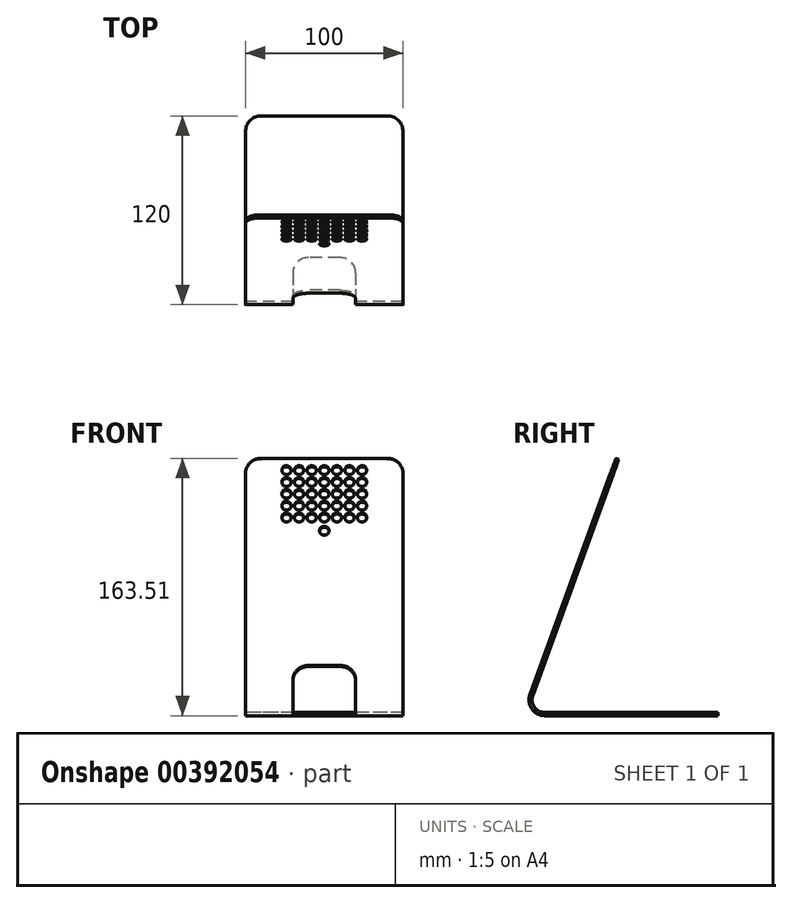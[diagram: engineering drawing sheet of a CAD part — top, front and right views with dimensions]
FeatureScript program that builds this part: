
annotation { "Feature Type Name" : "Feature", "Feature Type Description" : "" }
export const myFeature = defineFeature(function(context is Context, id is Id, definition is map)
    precondition{}
    {
        {
            var Q0;
            Q0=qCreatedBy(makeId("Right.planeOp"),FACE);
            var sketch = newSketch(context, id + "F0", { "sketchPlane" : qUnion([Q0])});
            skLineSegment(sketch, "E0", {"start": v(59.51, 163.5) * mm, "end": v(4.88, 13.42) * mm});
            skLineSegment(sketch, "E1", {"start": v(14.28, 0) * mm, "end": v(124.28, 0) * mm});
            skPoint(sketch, "E2.visualSharp", {"position": v(0, 0) * mm});
            skArc(sketch, "E2.filletArc", {"start": v(4.88, 13.42) * mm, "mid": v(6.09, 4.26) * mm, "end": v(14.28, 0) * mm});
            skLineSegment(sketch, "E3", {"start": v(4.28, 163.5) * mm, "end": v(4.28, 0) * mm, "construction": true});
            skLineSegment(sketch, "E4.0", {"start": v(14.28, 2) * mm, "end": v(124.28, 2) * mm});
            skArc(sketch, "E4.1", {"start": v(6.76, 12.74) * mm, "mid": v(7.73, 5.41) * mm, "end": v(14.28, 2) * mm});
            skLineSegment(sketch, "E4.2", {"start": v(61.4, 162.82) * mm, "end": v(6.76, 12.74) * mm});
            skLineSegment(sketch, "E5", {"start": v(59.51, 163.5) * mm, "end": v(61.4, 162.82) * mm});
            skLineSegment(sketch, "E6", {"start": v(124.28, 2) * mm, "end": v(124.28, 0) * mm});
            skSolve(sketch);
        }
        {
            var Q0;
            Q0 = qSketchRegion(id + "F0", true);
            extrude(context, id + "F1", {"entities" : qUnion([Q0]), "endBound" : BoundingType.SYMMETRIC, "depth" : 100 * mm});
        }
        {
            var Q0;
            Q0=makeQuery(id+"F1.opExtrude","CAP_EDGE",EDGE,{"disambiguationData":[OSD([sQuery(id+"F0.wireOp",EDGE,"E5")])],"isStart":true});
            var Q1;
            Q1=makeQuery(id+"F1.opExtrude","CAP_EDGE",EDGE,{"disambiguationData":[OSD([sQuery(id+"F0.wireOp",EDGE,"E5")])],"isStart":false});
            var Q2;
            Q2=makeQuery(id+"F1.opExtrude","CAP_EDGE",EDGE,{"disambiguationData":[OSD([sQuery(id+"F0.wireOp",EDGE,"E6")])],"isStart":false});
            var Q3;
            Q3=makeQuery(id+"F1.opExtrude","CAP_EDGE",EDGE,{"disambiguationData":[OSD([sQuery(id+"F0.wireOp",EDGE,"E6")])],"isStart":true});
            fillet(context, id + "F2", {"entities" : qUnion([Q0, Q1, Q2, Q3]), "radius" : 10 * mm, "tangentPropagation" : true, "allowEdgeOverflow" : false});
        }
        {
            var Q0;
            Q0=makeQuery(id+"F1.opExtrude","SWEPT_FACE",FACE,{"disambiguationData":[OSD([sQuery(id+"F0.wireOp",EDGE,"E0")])]});
            var sketch = newSketch(context, id + "F3", { "sketchPlane" : qUnion([Q0])});
            skPoint(sketch, "E7", {"position": v(0, 125) * mm});
            skSolve(sketch);
        }
        {
            var Q0;
            Q0=sQuery(id+"F3.wireOp",VERTEX,"E7");
            var Q1;
            Q1=makeQuery(id+"F1.opExtrude","SWEPT_BODY",BODY,{"disambiguationData":[OSD([sQuery(id+"F0.wireOp",EDGE,"E0"),sQuery(id+"F0.wireOp",EDGE,"E1"),sQuery(id+"F0.wireOp",EDGE,"E2.filletArc"),sQuery(id+"F0.wireOp",EDGE,"E4.0"),sQuery(id+"F0.wireOp",EDGE,"E4.1"),sQuery(id+"F0.wireOp",EDGE,"E4.2"),sQuery(id+"F0.wireOp",EDGE,"E5"),sQuery(id+"F0.wireOp",EDGE,"E6")])]});
            hole(context, id + "F4", {"style" : HoleStyle.SIMPLE, "endStyle" : HoleEndStyle.THROUGH, "holeDiameter" : 6 * mm, "isTappedThrough" : true, "tappedDepth" : 12 * mm, "tapClearance" : 3, "locations" : qUnion([Q0]), "scope" : qUnion([Q1])});
        }
        {
            var Q0;
            {var subQ0=sQuery(id+"F0.wireOp",EDGE,"E0");Q0=makeQuery(id+"F3.imprint","IMPRINT",FACE,{"disambiguationData":[TD([[makeQuery(id+"F3.imprint","IMPRINT",EDGE,{"derivedFrom":makeQuery(id+"F1.opExtrude","CAP_EDGE",EDGE,{"disambiguationData":[OSD([subQ0])],"isStart":true})}),1.0]])]});}
            var sketch = newSketch(context, id + "F5", { "sketchPlane" : qUnion([Q0])});
            skLineSegment(sketch, "E8.bottom", {"start": v(-28, 169) * mm, "end": v(28, 169) * mm, "construction": true});
            skLineSegment(sketch, "E8.top", {"start": v(-28, 131) * mm, "end": v(28, 131) * mm, "construction": true});
            skLineSegment(sketch, "E8.left", {"start": v(-28, 169) * mm, "end": v(-28, 131) * mm, "construction": true});
            skLineSegment(sketch, "E8.right", {"start": v(28, 169) * mm, "end": v(28, 131) * mm, "construction": true});
            skLineSegment(sketch, "E9", {"start": v(0, 169) * mm, "end": v(0, 131) * mm, "construction": true});
            skPoint(sketch, "E9.endSnap0", {"position": v(0, 131) * mm});
            skCircle(sketch, "E10", {"center": v(-24, 134) * mm, "radius": 3 * mm});
            skCircle(sketch, "E11.0.1.0", {"center": v(-24, 142) * mm, "radius": 3 * mm});
            skCircle(sketch, "E11.0.2.0", {"center": v(-24, 150) * mm, "radius": 3 * mm});
            skCircle(sketch, "E11.0.3.0", {"center": v(-24, 158) * mm, "radius": 3 * mm});
            skCircle(sketch, "E11.0.4.0", {"center": v(-24, 166) * mm, "radius": 3 * mm});
            skCircle(sketch, "E11.1.0.0", {"center": v(-16, 134) * mm, "radius": 3 * mm});
            skCircle(sketch, "E11.1.1.0", {"center": v(-16, 142) * mm, "radius": 3 * mm});
            skCircle(sketch, "E11.1.2.0", {"center": v(-16, 150) * mm, "radius": 3 * mm});
            skCircle(sketch, "E11.1.3.0", {"center": v(-16, 158) * mm, "radius": 3 * mm});
            skCircle(sketch, "E11.1.4.0", {"center": v(-16, 166) * mm, "radius": 3 * mm});
            skCircle(sketch, "E11.2.0.0", {"center": v(-8, 134) * mm, "radius": 3 * mm});
            skCircle(sketch, "E11.2.1.0", {"center": v(-8, 142) * mm, "radius": 3 * mm});
            skCircle(sketch, "E11.2.2.0", {"center": v(-8, 150) * mm, "radius": 3 * mm});
            skCircle(sketch, "E11.2.3.0", {"center": v(-8, 158) * mm, "radius": 3 * mm});
            skCircle(sketch, "E11.2.4.0", {"center": v(-8, 166) * mm, "radius": 3 * mm});
            skCircle(sketch, "E11.3.0.0", {"center": v(0, 134) * mm, "radius": 3 * mm});
            skCircle(sketch, "E11.3.1.0", {"center": v(0, 142) * mm, "radius": 3 * mm});
            skCircle(sketch, "E11.3.2.0", {"center": v(0, 150) * mm, "radius": 3 * mm});
            skCircle(sketch, "E11.3.3.0", {"center": v(0, 158) * mm, "radius": 3 * mm});
            skCircle(sketch, "E11.3.4.0", {"center": v(0, 166) * mm, "radius": 3 * mm});
            skCircle(sketch, "E11.4.0.0", {"center": v(8, 134) * mm, "radius": 3 * mm});
            skCircle(sketch, "E11.4.1.0", {"center": v(8, 142) * mm, "radius": 3 * mm});
            skCircle(sketch, "E11.4.2.0", {"center": v(8, 150) * mm, "radius": 3 * mm});
            skCircle(sketch, "E11.4.3.0", {"center": v(8, 158) * mm, "radius": 3 * mm});
            skCircle(sketch, "E11.4.4.0", {"center": v(8, 166) * mm, "radius": 3 * mm});
            skCircle(sketch, "E11.5.0.0", {"center": v(16, 134) * mm, "radius": 3 * mm});
            skCircle(sketch, "E11.5.1.0", {"center": v(16, 142) * mm, "radius": 3 * mm});
            skCircle(sketch, "E11.5.2.0", {"center": v(16, 150) * mm, "radius": 3 * mm});
            skCircle(sketch, "E11.5.3.0", {"center": v(16, 158) * mm, "radius": 3 * mm});
            skCircle(sketch, "E11.5.4.0", {"center": v(16, 166) * mm, "radius": 3 * mm});
            skCircle(sketch, "E11.6.0.0", {"center": v(24, 134) * mm, "radius": 3 * mm});
            skCircle(sketch, "E11.6.1.0", {"center": v(24, 142) * mm, "radius": 3 * mm});
            skCircle(sketch, "E11.6.2.0", {"center": v(24, 150) * mm, "radius": 3 * mm});
            skCircle(sketch, "E11.6.3.0", {"center": v(24, 158) * mm, "radius": 3 * mm});
            skCircle(sketch, "E11.6.4.0", {"center": v(24, 166) * mm, "radius": 3 * mm});
            skLineSegment(sketch, "E11.direction1", {"start": v(-24, 134) * mm, "end": v(-16, 134) * mm, "construction": true});
            skLineSegment(sketch, "E11.direction2", {"start": v(-24, 134) * mm, "end": v(-24, 142) * mm, "construction": true});
            skSolve(sketch);
        }
        {
            var Q0;
            Q0 = qSketchRegion(id + "F5", true);
            extrude(context, id + "F6", {"entities" : qUnion([Q0]), "operationType" : NewBodyOperationType.REMOVE, "endBound" : BoundingType.THROUGH_ALL, "oppositeDirection" : true, "depth" : 25 * mm});
        }
        {
            var Q0;
            {var subQ0=sQuery(id+"F0.wireOp",EDGE,"E0");Q0=makeQuery(id+"F3.imprint","IMPRINT",FACE,{"disambiguationData":[TD([[makeQuery(id+"F3.imprint","IMPRINT",EDGE,{"derivedFrom":makeQuery(id+"F1.opExtrude","CAP_EDGE",EDGE,{"disambiguationData":[OSD([subQ0])],"isStart":true})}),1.0]])]});}
            var sketch = newSketch(context, id + "F7", { "sketchPlane" : qUnion([Q0])});
            skLineSegment(sketch, "E12.bottom", {"start": v(-20, 34) * mm, "end": v(20, 34) * mm});
            skLineSegment(sketch, "E12.top", {"start": v(-20, 0) * mm, "end": v(20, 0) * mm});
            skLineSegment(sketch, "E12.left", {"start": v(-20, 34) * mm, "end": v(-20, 0) * mm});
            skLineSegment(sketch, "E12.right", {"start": v(20, 34) * mm, "end": v(20, 0) * mm});
            skLineSegment(sketch, "E13", {"start": v(0, 34) * mm, "end": v(0, 0) * mm, "construction": true});
            skSolve(sketch);
        }
        {
            var Q0;
            Q0 = qSketchRegion(id + "F7", true);
            extrude(context, id + "F8", {"entities" : qUnion([Q0]), "operationType" : NewBodyOperationType.REMOVE, "oppositeDirection" : true, "depth" : 20 * mm});
        }
        {
            var Q0;
            Q0=makeQuery(id+"F1.opExtrude","SWEPT_FACE",FACE,{"disambiguationData":[OSD([sQuery(id+"F0.wireOp",EDGE,"E1")])]});
            var sketch = newSketch(context, id + "F9", { "sketchPlane" : qUnion([Q0])});
            skLineSegment(sketch, "E14.bottom", {"start": v(-20, -34.28) * mm, "end": v(20, -34.28) * mm});
            skLineSegment(sketch, "E14.top", {"start": v(-20, -4.28) * mm, "end": v(20, -4.28) * mm});
            skLineSegment(sketch, "E14.left", {"start": v(-20, -34.28) * mm, "end": v(-20, -4.28) * mm});
            skLineSegment(sketch, "E14.right", {"start": v(20, -34.28) * mm, "end": v(20, -4.28) * mm});
            skLineSegment(sketch, "E15", {"start": v(0, -4.28) * mm, "end": v(0, -34.28) * mm, "construction": true});
            skSolve(sketch);
        }
        {
            var Q0;
            Q0 = qSketchRegion(id + "F9", true);
            extrude(context, id + "F10", {"entities" : qUnion([Q0]), "operationType" : NewBodyOperationType.REMOVE, "oppositeDirection" : true, "depth" : 10 * mm});
        }
        {
            var Q0;
            Q0=makeQuery(id+"F8.boolean.opBoolean","COPY",EDGE,{"derivedFrom":makeQuery(id+"F8.opExtrude","SWEPT_EDGE",EDGE,{"disambiguationData":[OSD([sQuery(id+"F7.wireOp",EDGE,"E12.bottom"),sQuery(id+"F7.wireOp",EDGE,"E12.left")])]})});
            var Q1;
            Q1=makeQuery(id+"F10.boolean.opBoolean","COPY",EDGE,{"derivedFrom":makeQuery(id+"F10.opExtrude","SWEPT_EDGE",EDGE,{"disambiguationData":[OSD([sQuery(id+"F9.wireOp",EDGE,"E14.bottom"),sQuery(id+"F9.wireOp",EDGE,"E14.left")])]})});
            var Q2;
            Q2=makeQuery(id+"F8.boolean.opBoolean","COPY",EDGE,{"derivedFrom":makeQuery(id+"F8.opExtrude","SWEPT_EDGE",EDGE,{"disambiguationData":[OSD([sQuery(id+"F7.wireOp",EDGE,"E12.bottom"),sQuery(id+"F7.wireOp",EDGE,"E12.right")])]})});
            var Q3;
            Q3=makeQuery(id+"F10.boolean.opBoolean","COPY",EDGE,{"derivedFrom":makeQuery(id+"F10.opExtrude","SWEPT_EDGE",EDGE,{"disambiguationData":[OSD([sQuery(id+"F9.wireOp",EDGE,"E14.bottom"),sQuery(id+"F9.wireOp",EDGE,"E14.right")])]})});
            fillet(context, id + "F11", {"entities" : qUnion([Q0, Q1, Q2, Q3]), "radius" : 10 * mm, "tangentPropagation" : true, "allowEdgeOverflow" : false});
        }
    });
